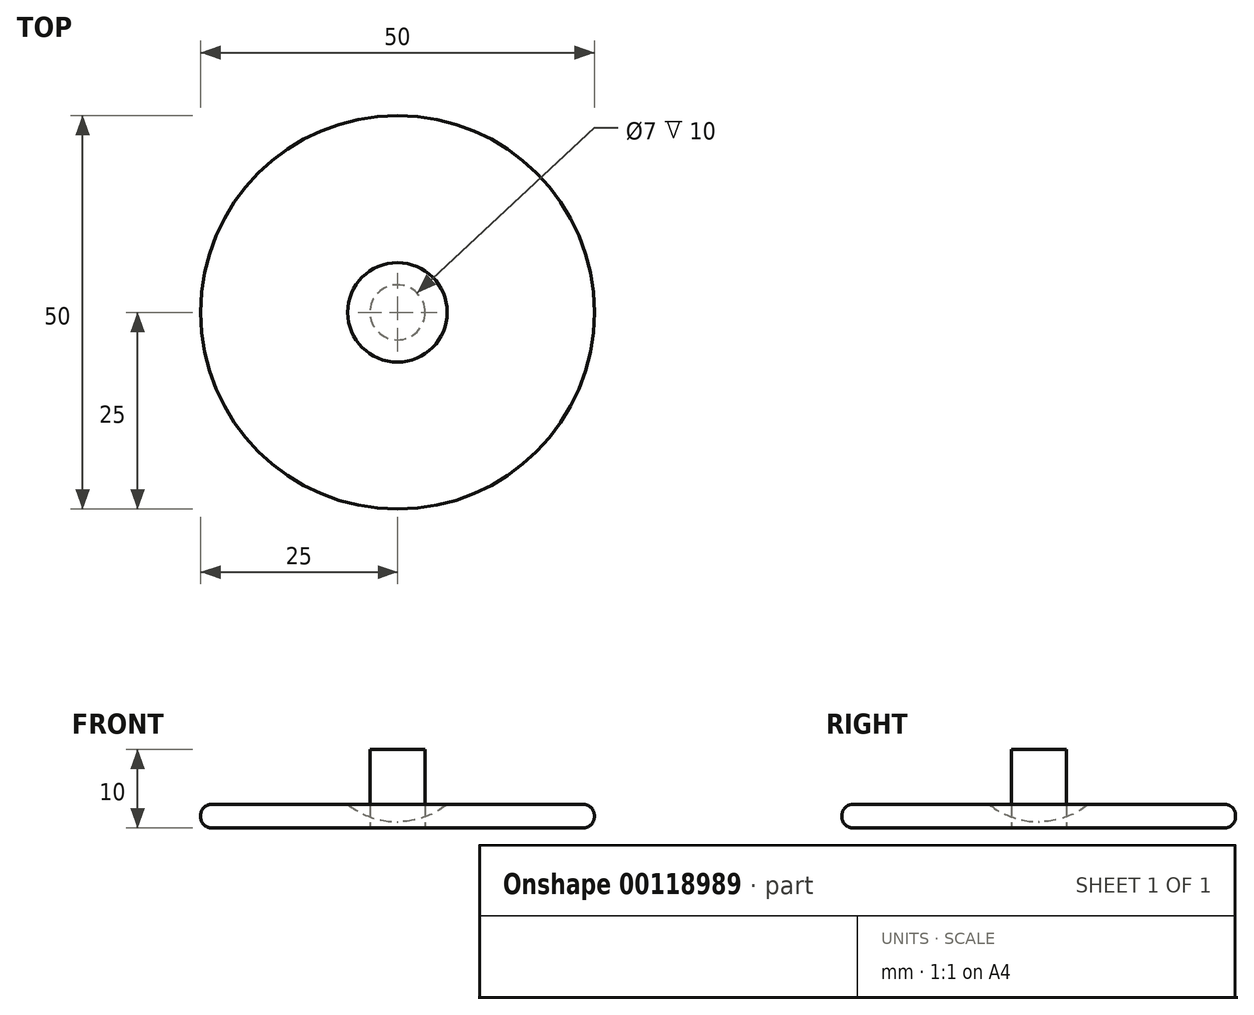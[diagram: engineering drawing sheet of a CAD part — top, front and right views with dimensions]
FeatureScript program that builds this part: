
annotation { "Feature Type Name" : "Feature", "Feature Type Description" : "" }
export const myFeature = defineFeature(function(context is Context, id is Id, definition is map)
    precondition{}
    {
        {
            var Q0;
            Q0=qCreatedBy(makeId("Top.planeOp"),FACE);
            var sketch = newSketch(context, id + "F0", { "sketchPlane" : qUnion([Q0])});
            skCircle(sketch, "E0", {"center": v(0, 0) * mm, "radius": 25 * mm});
            skSolve(sketch);
        }
        {
            var Q0;
            Q0=qSketchRegion(id+"F0",true);
            extrude(context, id + "F1", {"entities" : qUnion([Q0]), "depth" : 3 * mm});
        }
        {
            var Q0;
            Q0=qCreatedBy(makeId("Front.planeOp"),FACE);
            var sketch = newSketch(context, id + "F2", { "sketchPlane" : qUnion([Q0])});
            skArc(sketch, "E1", {"start": v(0, 0.8) * mm, "mid": v(10.05, 10.8) * mm, "end": v(0, 20.8) * mm});
            skLineSegment(sketch, "E2", {"start": v(0, 10.15) * mm, "end": v(0, 20.8) * mm});
            skLineSegment(sketch, "E3", {"start": v(0, 0.8) * mm, "end": v(0, 10.15) * mm});
            skSolve(sketch);
        }
        {
            var Q0;
            {var subQ0=sQuery(id+"F2.wireOp",EDGE,"E1");Q0=makeQuery(id+"F2.imprint","IMPRINT",FACE,{"disambiguationData":[TD([[makeQuery(id+"F2.imprint","IMPRINT",EDGE,{"derivedFrom":subQ0}),1.0]])]});}
            var Q1;
            Q1=sQuery(id+"F2.wireOp",EDGE,"E3");
            revolve(context, id + "F3", {"operationType" : NewBodyOperationType.ADD, "entities" : qUnion([Q0]), "axis" : qUnion([Q1]), "revolveType" : RevolveType.FULL});
        }
        {
            var Q0;
            Q0=makeQuery(id+"F1.opExtrude","CAP_EDGE",EDGE,{"disambiguationData":[OSD([sQuery(id+"F0.wireOp",EDGE,"E0")])],"isStart":true});
            var Q1;
            Q1=makeQuery(id+"F1.opExtrude","CAP_EDGE",EDGE,{"disambiguationData":[OSD([sQuery(id+"F0.wireOp",EDGE,"E0")])],"isStart":false});
            fillet(context, id + "F4", {"entities" : qUnion([Q0, Q1]), "radius" : 1.4 * mm, "tangentPropagation" : true, "allowEdgeOverflow" : false});
        }
        {
            var Q0;
            Q0=makeQuery(id+"F1.opExtrude","CAP_FACE",FACE,{"disambiguationData":[OSD([sQuery(id+"F0.wireOp",EDGE,"E0")])],"isStart":true});
            var sketch = newSketch(context, id + "F5", { "sketchPlane" : qUnion([Q0])});
            skCircle(sketch, "E4", {"center": v(0, 0) * mm, "radius": 3.5 * mm});
            skSolve(sketch);
        }
        {
            var Q0;
            Q0 = qSketchRegion(id + "F5", true);
            extrude(context, id + "F6", {"entities" : qUnion([Q0]), "operationType" : NewBodyOperationType.REMOVE, "oppositeDirection" : true, "depth" : 10 * mm});
        }
    });
